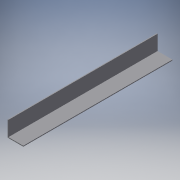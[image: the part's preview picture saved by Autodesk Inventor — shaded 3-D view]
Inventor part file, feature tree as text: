
AUTODESK INVENTOR PART (.ipt)
format: ipt  version: 2017 (Build 210142000, 142)  size: 101,376 bytes
history: native  units: in
note: dims shown in document units (in); Inventor stores cm internally (conversion verified against a paired STEP export)
features: extrude x2, sketch x2
ambient origin geometry x8: Origin, YZ Plane, XZ Plane, XY Plane, X Axis, Y Axis, Z Axis, Center Point
bodies: Solid1 (feature_tree)
feature tree (4):
  extrude  "Extrusion1"  Depth=1.32in
  extrude  "Extrusion2"  Depth=0.07in
  sketch  "Sketch1"  dims[d0=12.5in d1=1.32in]
  sketch  "Sketch2"  dims[d2=0.07in d3=0.0in d4=0.07in d5=1.25in d6=0.0in]
